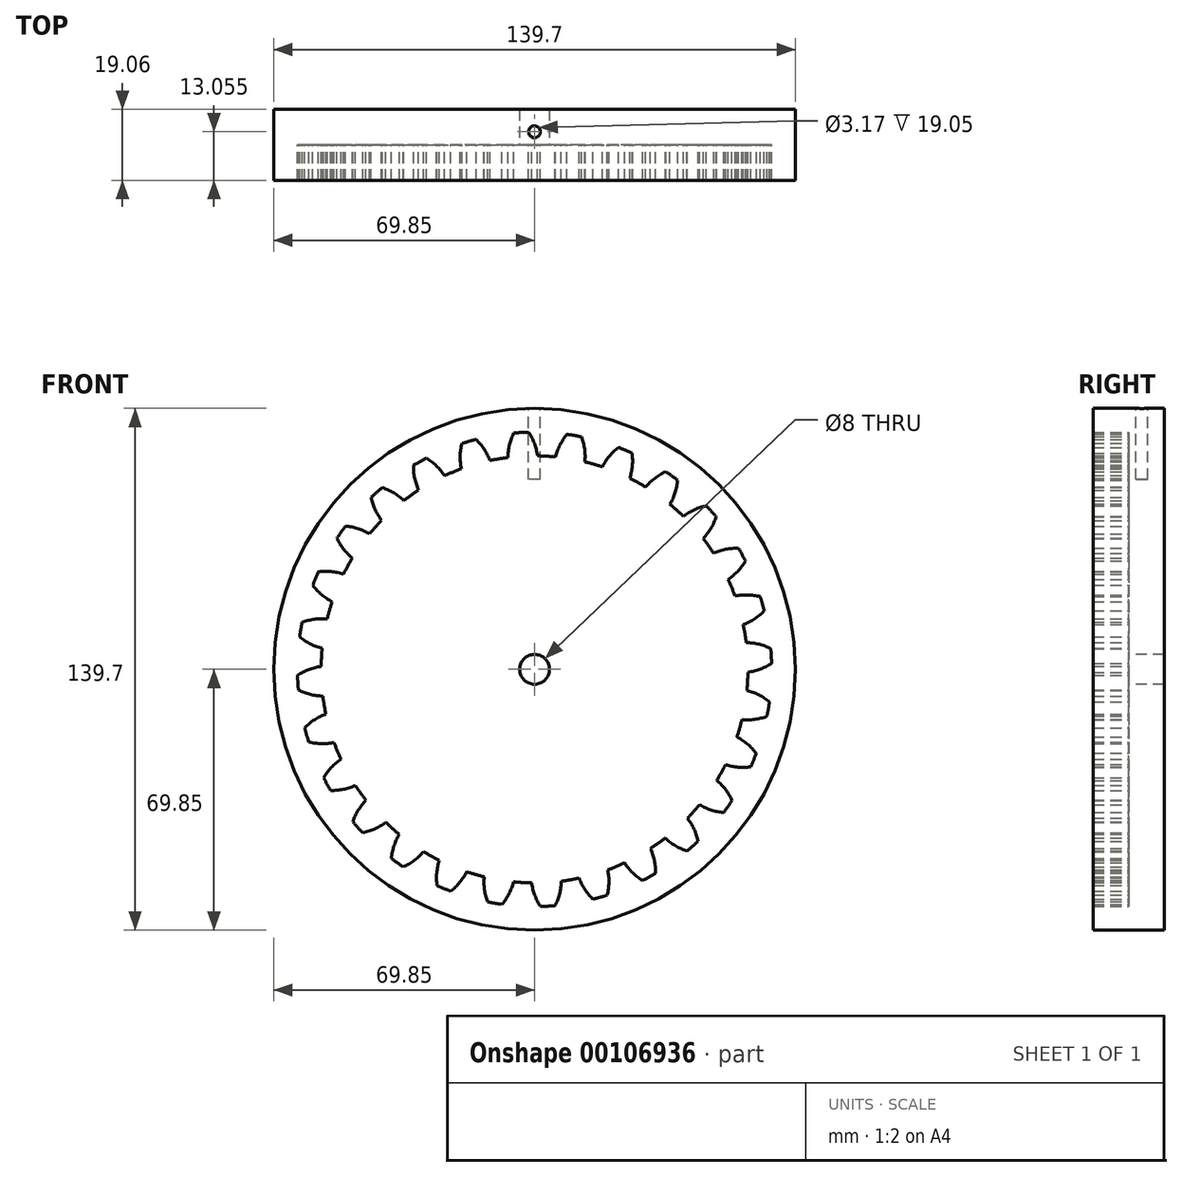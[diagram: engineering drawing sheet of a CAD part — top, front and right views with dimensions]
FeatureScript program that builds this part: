
annotation { "Feature Type Name" : "Feature", "Feature Type Description" : "" }
export const myFeature = defineFeature(function(context is Context, id is Id, definition is map)
    precondition{}
    {
        {
            var Q0;
            Q0=qCreatedBy(makeId("Front.planeOp"),FACE);
            var sketch = newSketch(context, id + "F0", { "sketchPlane" : qUnion([Q0])});
            skCircle(sketch, "E0", {"center": v(0, 0) * mm, "radius": 63.5 * mm, "construction": true});
            skCircle(sketch, "E1", {"center": v(0, 0) * mm, "radius": 60.33 * mm, "construction": true});
            skCircle(sketch, "E2", {"center": v(0, 0) * mm, "radius": 57.15 * mm, "construction": true});
            skLineSegment(sketch, "E3", {"start": v(0, 0) * mm, "end": v(0, 97.64) * mm, "construction": true});
            skLineSegment(sketch, "E4", {"start": v(0, 0) * mm, "end": v(-5.72, 102.06) * mm, "construction": true});
            skLineSegment(sketch, "E5", {"start": v(0, 60.33) * mm, "end": v(-61, 60.32) * mm, "construction": true});
            skLineSegment(sketch, "E6", {"start": v(0, 60.33) * mm, "end": v(-47.6, 43) * mm, "construction": true});
            skCircle(sketch, "E7", {"center": v(0, 60.33) * mm, "radius": 15.11 * mm, "construction": true});
            skCircle(sketch, "E8", {"center": v(-14.2, 55.16) * mm, "radius": 15.11 * mm, "construction": true});
            skArc(sketch, "E9", {"start": v(0.78, 57.14) * mm, "mid": v(-0.04, 60.45) * mm, "end": v(-1.59, 63.48) * mm});
            skArc(sketch, "E10.MirrorCS", {"start": v(-7.16, 56.7) * mm, "mid": v(-6.71, 60.07) * mm, "end": v(-5.52, 63.26) * mm});
            skArc(sketch, "E11", {"start": v(-1.59, 63.48) * mm, "mid": v(-3.56, 63.4) * mm, "end": v(-5.52, 63.26) * mm});
            skArc(sketch, "E12", {"start": v(0.78, 57.14) * mm, "mid": v(-3.2, 57.06) * mm, "end": v(-7.16, 56.7) * mm});
            skLineSegment(sketch, "E13", {"start": v(-7.16, 56.7) * mm, "end": v(0.78, 57.14) * mm, "construction": true});
            skSolve(sketch);
        }
        {
            var Q0;
            Q0=makeQuery(id+"F0.imprint","IMPRINT",FACE,{"disambiguationData":[TD([[makeQuery(id+"F0.imprint","IMPRINT",EDGE,{"derivedFrom":sQuery(id+"F0.wireOp",EDGE,"E9")}),1.0]])]});
            extrude(context, id + "F1", {"entities" : qUnion([Q0]), "depth" : 9.52 * mm});
        }
        {
            var Q0;
            Q0=makeQuery(id+"F1.opExtrude","SWEPT_BODY",BODY,{"disambiguationData":[OSD([sQuery(id+"F0.wireOp",EDGE,"E9"),sQuery(id+"F0.wireOp",EDGE,"E10.MirrorCS"),sQuery(id+"F0.wireOp",EDGE,"E11"),sQuery(id+"F0.wireOp",EDGE,"E12")])]});
            var Q1;
            Q1=sQuery(id+"F0.wireOp",EDGE,"E2");
            circularPattern(context, id + "F2", {"entities" : qUnion([Q0]), "axis" : qUnion([Q1]), "angle" : 360 * degree, "instanceCount" : 28, "equalSpace" : true});
        }
        {
            var Q0;
            Q0=qCreatedBy(makeId("Front.planeOp"),FACE);
            var sketch = newSketch(context, id + "F3", { "sketchPlane" : qUnion([Q0])});
            skCircle(sketch, "E14.0", {"center": v(0, 0) * mm, "radius": 57.15 * mm});
            skSolve(sketch);
        }
        {
            var Q0;
            Q0=makeQuery(id+"F3.imprint","IMPRINT",FACE,{"disambiguationData":[TD([[makeQuery(id+"F3.imprint","IMPRINT",EDGE,{"derivedFrom":sQuery(id+"F3.wireOp",EDGE,"E14.0")}),1.0]])]});
            var Q1;
            Q1=makeQuery(id+"F2.opPattern","COPY",FACE,{"derivedFrom":makeQuery(id+"F1.opExtrude","CAP_FACE",FACE,{"disambiguationData":[OSD([sQuery(id+"F0.wireOp",EDGE,"E9"),sQuery(id+"F0.wireOp",EDGE,"E10.MirrorCS"),sQuery(id+"F0.wireOp",EDGE,"E11"),sQuery(id+"F0.wireOp",EDGE,"E12")])],"isStart":false}),"instanceName":"9"});
            extrude(context, id + "F4", {"entities" : qUnion([Q0]), "operationType" : NewBodyOperationType.ADD, "endBound" : BoundingType.UP_TO_SURFACE, "endBoundEntityFace" : qUnion([Q1]), "depth" : 25.4 * mm});
        }
        {
            var Q0;
            Q0=qCreatedBy(makeId("Front.planeOp"),FACE);
            var sketch = newSketch(context, id + "F5", { "sketchPlane" : qUnion([Q0])});
            skCircle(sketch, "E15", {"center": v(0, 0) * mm, "radius": 69.85 * mm});
            skSolve(sketch);
        }
        {
            var Q0;
            Q0=makeQuery(id+"F5.imprint","IMPRINT",FACE,{"disambiguationData":[TD([[makeQuery(id+"F5.imprint","IMPRINT",EDGE,{"derivedFrom":sQuery(id+"F5.wireOp",EDGE,"E15")}),1.0]])]});
            extrude(context, id + "F6", {"entities" : qUnion([Q0]), "depth" : 9.52 * mm, "hasSecondDirection" : true, "secondDirectionOppositeDirection" : true, "secondDirectionDepth" : 9.52 * mm});
        }
        {
            var Q0;
            Q0=makeQuery(id+"F1.opExtrude","SWEPT_BODY",BODY,{"disambiguationData":[OSD([sQuery(id+"F0.wireOp",EDGE,"E9"),sQuery(id+"F0.wireOp",EDGE,"E10.MirrorCS"),sQuery(id+"F0.wireOp",EDGE,"E11"),sQuery(id+"F0.wireOp",EDGE,"E12")])]});
            var Q1;
            Q1=makeQuery(id+"F6.opExtrude","SWEPT_BODY",BODY,{"disambiguationData":[OSD([sQuery(id+"F5.wireOp",EDGE,"E15")])]});
            booleanBodies(context, id + "F7", {"operationType" : BooleanOperationType.SUBTRACTION, "tools" : qUnion([Q0]), "targets" : qUnion([Q1])});
        }
        {
            var Q0;
            {var subQ0=makeQuery(id+"F1.opExtrude","CAP_FACE",FACE,{"disambiguationData":[OSD([sQuery(id+"F0.wireOp",EDGE,"E9"),sQuery(id+"F0.wireOp",EDGE,"E10.MirrorCS"),sQuery(id+"F0.wireOp",EDGE,"E11"),sQuery(id+"F0.wireOp",EDGE,"E12")])],"isStart":true});Q0=makeQuery(id+"F7.opBoolean","COPY",FACE,{"derivedFrom":makeQuery(id+"F4.boolean.opBoolean","MERGE",FACE,{"derivedFrom":[subQ0,makeQuery(id+"F2.opPattern","COPY",FACE,{"derivedFrom":subQ0,"instanceName":"1"}),makeQuery(id+"F2.opPattern","COPY",FACE,{"derivedFrom":subQ0,"instanceName":"2"}),makeQuery(id+"F2.opPattern","COPY",FACE,{"derivedFrom":subQ0,"instanceName":"3"}),makeQuery(id+"F2.opPattern","COPY",FACE,{"derivedFrom":subQ0,"instanceName":"4"}),makeQuery(id+"F2.opPattern","COPY",FACE,{"derivedFrom":subQ0,"instanceName":"5"}),makeQuery(id+"F2.opPattern","COPY",FACE,{"derivedFrom":subQ0,"instanceName":"6"}),makeQuery(id+"F2.opPattern","COPY",FACE,{"derivedFrom":subQ0,"instanceName":"7"}),makeQuery(id+"F2.opPattern","COPY",FACE,{"derivedFrom":subQ0,"instanceName":"8"}),makeQuery(id+"F2.opPattern","COPY",FACE,{"derivedFrom":subQ0,"instanceName":"9"}),makeQuery(id+"F2.opPattern","COPY",FACE,{"derivedFrom":subQ0,"instanceName":"10"}),makeQuery(id+"F2.opPattern","COPY",FACE,{"derivedFrom":subQ0,"instanceName":"11"}),makeQuery(id+"F2.opPattern","COPY",FACE,{"derivedFrom":subQ0,"instanceName":"12"}),makeQuery(id+"F2.opPattern","COPY",FACE,{"derivedFrom":subQ0,"instanceName":"13"}),makeQuery(id+"F2.opPattern","COPY",FACE,{"derivedFrom":subQ0,"instanceName":"14"}),makeQuery(id+"F2.opPattern","COPY",FACE,{"derivedFrom":subQ0,"instanceName":"15"}),makeQuery(id+"F2.opPattern","COPY",FACE,{"derivedFrom":subQ0,"instanceName":"16"}),makeQuery(id+"F2.opPattern","COPY",FACE,{"derivedFrom":subQ0,"instanceName":"17"}),makeQuery(id+"F2.opPattern","COPY",FACE,{"derivedFrom":subQ0,"instanceName":"18"}),makeQuery(id+"F2.opPattern","COPY",FACE,{"derivedFrom":subQ0,"instanceName":"19"}),makeQuery(id+"F2.opPattern","COPY",FACE,{"derivedFrom":subQ0,"instanceName":"20"}),makeQuery(id+"F2.opPattern","COPY",FACE,{"derivedFrom":subQ0,"instanceName":"21"}),makeQuery(id+"F2.opPattern","COPY",FACE,{"derivedFrom":subQ0,"instanceName":"22"}),makeQuery(id+"F2.opPattern","COPY",FACE,{"derivedFrom":subQ0,"instanceName":"23"}),makeQuery(id+"F2.opPattern","COPY",FACE,{"derivedFrom":subQ0,"instanceName":"24"}),makeQuery(id+"F2.opPattern","COPY",FACE,{"derivedFrom":subQ0,"instanceName":"25"}),makeQuery(id+"F2.opPattern","COPY",FACE,{"derivedFrom":subQ0,"instanceName":"26"}),makeQuery(id+"F2.opPattern","COPY",FACE,{"derivedFrom":subQ0,"instanceName":"27"}),makeQuery(id+"F4.opExtrude","CAP_FACE",FACE,{"disambiguationData":[OSD([sQuery(id+"F3.wireOp",EDGE,"E14.0")])],"isStart":true})]})});}
            var sketch = newSketch(context, id + "F8", { "sketchPlane" : qUnion([Q0])});
            skCircle(sketch, "E16", {"center": v(0, 0) * mm, "radius": 4 * mm});
            skSolve(sketch);
        }
        {
            var Q0;
            Q0 = qSketchRegion(id + "F8", true);
            extrude(context, id + "F9", {"entities" : qUnion([Q0]), "operationType" : NewBodyOperationType.REMOVE, "endBound" : BoundingType.THROUGH_ALL, "oppositeDirection" : true, "depth" : 25.4 * mm});
        }
        {
            var Q0;
            Q0=qCreatedBy(makeId("Top.planeOp"),FACE);
            cPlane(context, id + "F10", {"entities" : qUnion([Q0]), "cplaneType" : CPlaneType.OFFSET, "offset" : 76.2 * mm, "width" : 152.4 * mm, "height" : 152.4 * mm});
        }
        {
            var Q0;
            Q0=qCreatedBy(id+"F10.planeOp",FACE);
            var sketch = newSketch(context, id + "F11", { "sketchPlane" : qUnion([Q0])});
            skCircle(sketch, "E17", {"center": v(0, 3.53) * mm, "radius": 1.59 * mm});
            skSolve(sketch);
        }
        {
            var Q0;
            Q0=makeQuery(id+"F11.imprint","IMPRINT",FACE,{"disambiguationData":[TD([[makeQuery(id+"F11.imprint","IMPRINT",EDGE,{"derivedFrom":sQuery(id+"F11.wireOp",EDGE,"E17")}),1.0]])]});
            extrude(context, id + "F12", {"entities" : qUnion([Q0]), "operationType" : NewBodyOperationType.REMOVE, "oppositeDirection" : true, "depth" : 25.4 * mm});
        }
    });
